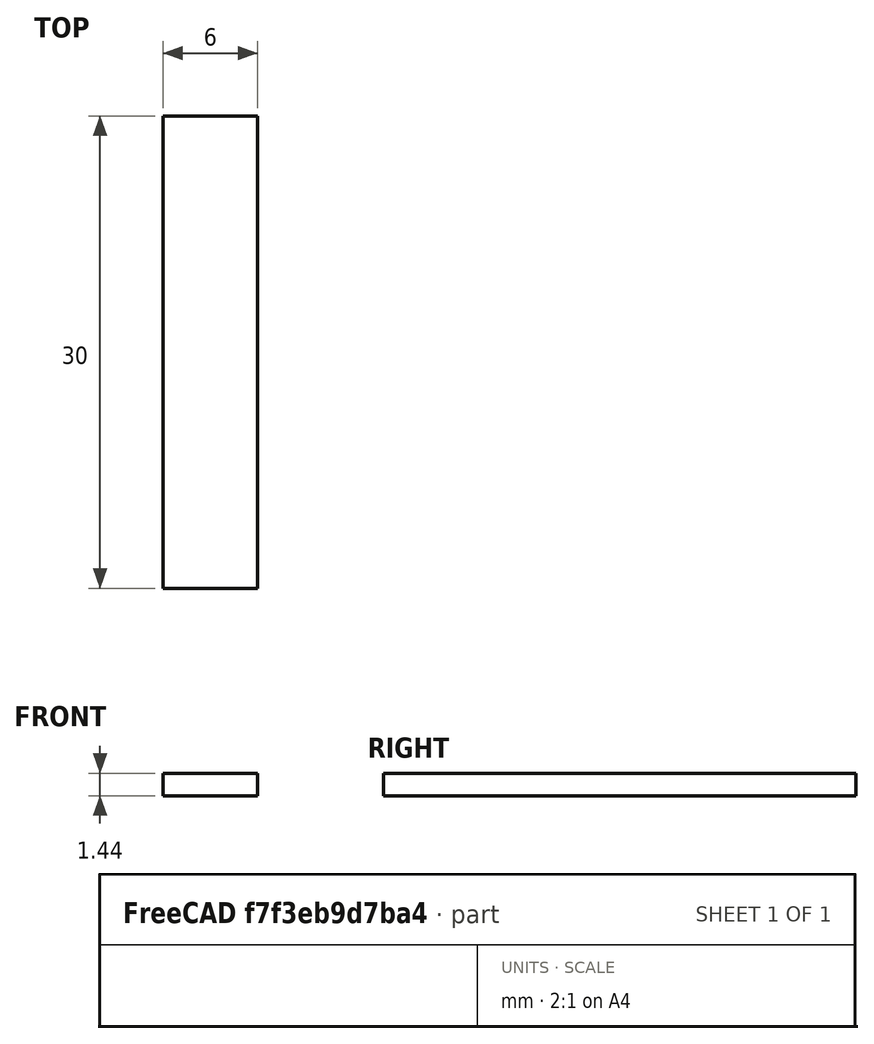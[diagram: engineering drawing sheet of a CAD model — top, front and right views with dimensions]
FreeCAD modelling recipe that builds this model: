
FCSTD DOCUMENT  (FreeCAD 0.21R33771 (Git))
Label: black_key_bottom
License: All rights reserved
LicenseURL: http://en.wikipedia.org/wiki/All_rights_reserved
objects: Sketcher::SketchObject×1, PartDesign::Pad×1, PartDesign::Body×1
note: 4 computed .brp shape members not serialized (recipe doc carries the construction recipe); baked Part::Feature solids carry a one-line shape summary decoded from their .brp

FEATURE [Sketcher::SketchObject] Sketch
  FullyConstrained = true
  sketch-geometry (4):
    g0: LineSegment StartX=0 StartY=0 StartZ=0 EndX=6 EndY=0 EndZ=0
    g1: LineSegment StartX=6 StartY=0 StartZ=0 EndX=6 EndY=30 EndZ=0
    g2: LineSegment StartX=6 StartY=30 StartZ=0 EndX=0 EndY=30 EndZ=0
    g3: LineSegment StartX=0 StartY=30 StartZ=0 EndX=0 EndY=0 EndZ=0
  constraints (11):
    c: Coincident(g0,g1)
    c: Coincident(g1,g2)
    c: Coincident(g2,g3)
    c: Coincident(g3,g0)
    c: Horizontal(g0)
    c: Horizontal(g2)
    c: Vertical(g1)
    c: Vertical(g3)
    c: Coincident(g0,g-1)
    c: DistanceX(g2,g2) = 6
    c: DistanceY(g1,g1) = 30
FEATURE [PartDesign::Pad] Pad
  Direction = (0,0,1)
  Length = 0.63
  Length2 = 10
  Profile = -> Sketch
  ReferenceAxis = -> Sketch [N_Axis]
  Type = 0
  expr: Length = 1.44 - 0.81
FEATURE [PartDesign::Body] Body
  Group = -> [Sketch,Pad]
  Origin = -> Origin
  Tip = -> Pad
